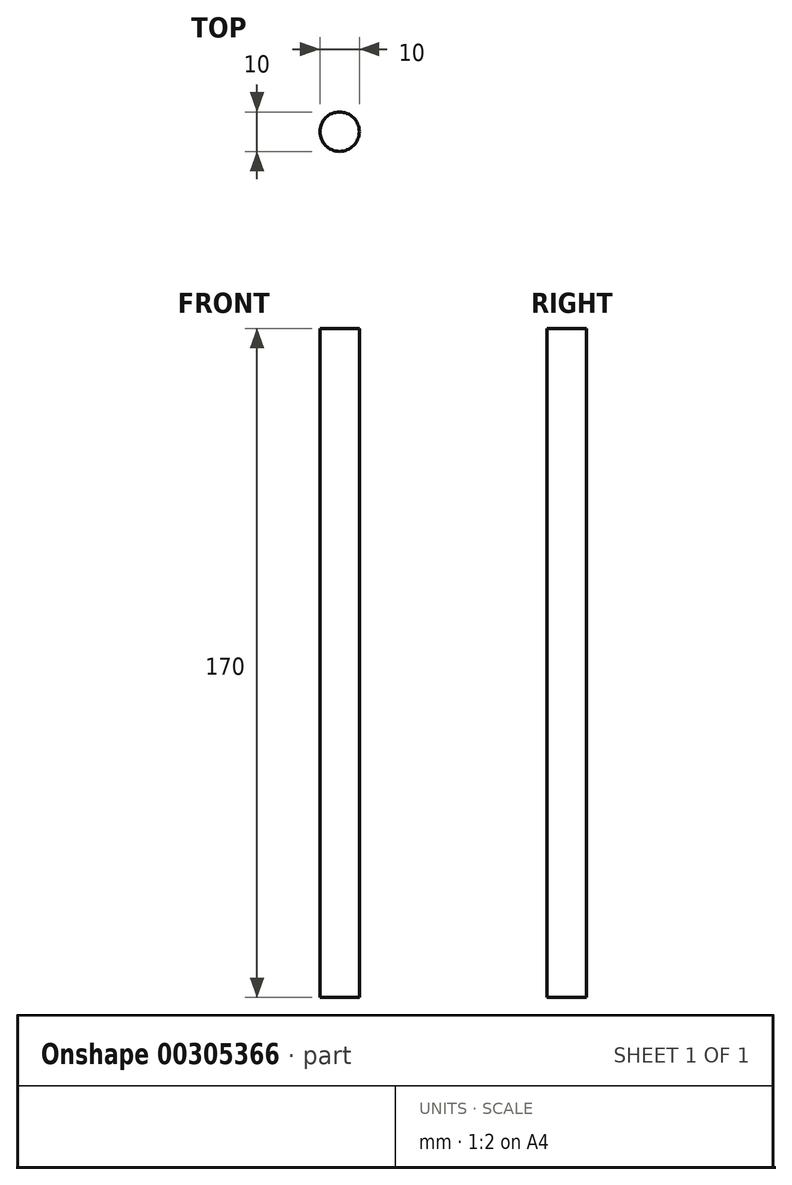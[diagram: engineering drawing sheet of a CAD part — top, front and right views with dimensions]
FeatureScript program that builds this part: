
annotation { "Feature Type Name" : "Feature", "Feature Type Description" : "" }
export const myFeature = defineFeature(function(context is Context, id is Id, definition is map)
    precondition{}
    {
        {
            var Q0;
            Q0=qCreatedBy(makeId("Top.planeOp"),FACE);
            var sketch = newSketch(context, id + "F0", { "sketchPlane" : qUnion([Q0])});
            skCircle(sketch, "E0", {"center": v(0, 0) * mm, "radius": 5 * mm});
            skSolve(sketch);
        }
        {
            var Q0;
            Q0=qSketchRegion(id+"F0",true);
            extrude(context, id + "F1", {"entities" : qUnion([Q0]), "depth" : 170 * mm});
        }
    });
